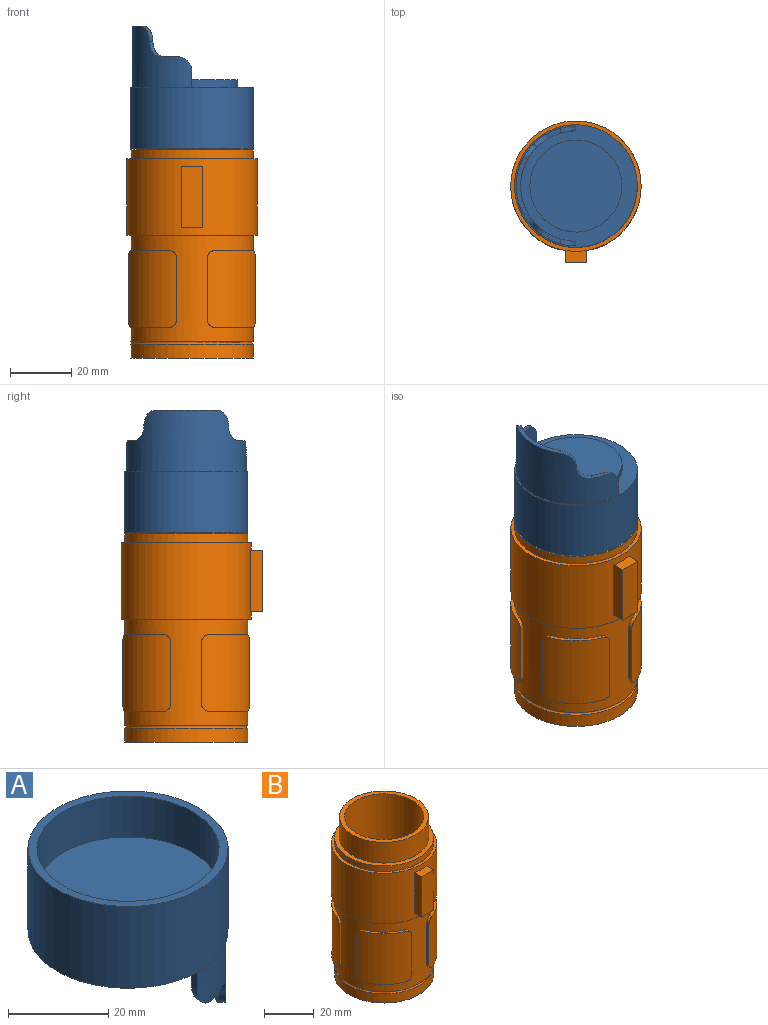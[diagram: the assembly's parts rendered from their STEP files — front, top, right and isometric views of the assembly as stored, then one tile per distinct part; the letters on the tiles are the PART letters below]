
ASSEMBLY  parts=2 mates=1
PART A: 20 faces, bbox 40x40x40 mm
  f0: plane 40x40mm, normal (0,0,-1), area 461.4mm2, adj f1,f5,f6,f8,f10,f18
  f1: cylinder r=20mm len=40mm, axis (0,0,-1), area 2513.3mm2, adj f0,f3
  f2: cylinder r=18.2mm len=36.4mm, axis (0,0,-1), area 1143.5mm2, adj f3,f4
  f3: plane 40x40mm, normal (0,0,1), area 216mm2, adj f1,f2
  f4: plane 36.4x36.4mm, normal (0,0,1), area 1040.6mm2, adj f2
  f5: cylinder r=18mm len=36mm, axis (0,0,1), area 837.5mm2, adj f0,f7,f8,f9,f10,f11,f12,f13
  f6: cylinder r=19.5mm len=39mm, axis (0,0,1), area 908.2mm2, adj f0,f7,f8,f9,f10,f11,f12,f13
  f7: plane 19.58x3.74mm, normal (0,0,-1), area 29mm2, adj f5,f6,f12,f16
  f8: plane 5x1.5mm, normal (-1,0,0), area 7.5mm2, adj f0,f5,f6,f14
  f9: plane 4.79x3.09mm, normal (0,0,-1), area 6.9mm2, adj f5,f6,f13,f14
  f10: plane 5x1.5mm, normal (-1,0,0), area 7.5mm2, adj f0,f5,f6,f15
  f11: plane 4.79x3.09mm, normal (0,0,-1), area 6.9mm2, adj f5,f6,f15,f17
  f12: cylinder r=5mm len=5.1mm, axis (0.71,-0.71,0), area 11.9mm2, adj f5,f6,f7,f13
  f13: cylinder r=5mm len=5.1mm, axis (-0.71,0.71,0), area 11.9mm2, adj f5,f6,f9,f12
  f14: cylinder r=5mm len=5mm, axis (0,-1,0), area 11.9mm2, adj f5,f6,f8,f9
  f15: cylinder r=5mm len=5mm, axis (0,-1,0), area 11.9mm2, adj f5,f6,f10,f11
  f16: cylinder r=5mm len=5.1mm, axis (-0.71,-0.71,0), area 11.9mm2, adj f5,f6,f7,f17
  f17: cylinder r=5mm len=5.1mm, axis (0.71,0.71,0), area 11.9mm2, adj f5,f6,f11,f16
  f18: cylinder r=15mm len=30mm, axis (0,0,1), area 235.6mm2, adj f0,f19
  f19: plane 30x30mm, normal (0,0,-1), area 706.9mm2, adj f18
PART B: 54 faces, bbox 44.1x47x78 mm
  f0: cylinder r=20mm len=40mm, axis (0,0,-1), area 351.9mm2, adj f5,f7
  f1: plane 36x36mm, normal (0,0,1), area 213.6mm2, adj f2,f4
  f2: cylinder r=16mm len=74mm, axis (0,0,-1), area 7439.3mm2, adj f1,f3
  f3: plane 32x32mm, normal (0,0,1), area 804.2mm2, adj f2
  f4: cylinder r=18mm len=36mm, axis (0,0,1), area 1153.6mm2, adj f1,f5
  f5: plane 40x40mm, normal (0,0,1), area 238.8mm2, adj f0,f4
  f6: cylinder r=21.25mm len=42.5mm, axis (0,0,-1), area 3197.3mm2, adj f7,f8,f49,f50,f51,f52
  f7: plane 42.5x42.5mm, normal (0,0,1), area 162mm2, adj f0,f6
  f8: plane 42.5x42.5mm, normal (0,0,-1), area 162mm2, adj f6,f48
  f9: plane 40x40mm, normal (0,0,-1), area 1256.6mm2, adj f14
  f10: cylinder r=21.25mm len=25mm, axis (0,0,-1), area 576.6mm2, adj f15,f16,f17,f18,f19,f20,f21,f22
  f11: cylinder r=21.25mm len=25mm, axis (0,0,-1), area 576.6mm2, adj f23,f24,f25,f26,f27,f28,f29,f30
  f12: cylinder r=21.25mm len=25mm, axis (0,0,-1), area 576.6mm2, adj f31,f32,f33,f34,f35,f36,f37,f38
  f13: cylinder r=21.25mm len=25mm, axis (0,0,-1), area 576.6mm2, adj f39,f40,f41,f42,f43,f44,f45,f46
  f14: cylinder r=20mm len=40mm, axis (0,0,-1), area 565.5mm2, adj f9,f47
  f15: cylinder r=2.5mm len=2.5mm, axis (0,-1,0), area 5.1mm2, adj f10,f16,f22,f48
  f16: plane 12.38x12.38mm, normal (0,0,-1), area 21.3mm2, adj f10,f15,f17,f48
  f17: cylinder r=2.5mm len=2.5mm, axis (-1,0,0), area 5.1mm2, adj f10,f16,f18,f48
  f18: plane 20x1.29mm, normal (0,1,0), area 25.8mm2, adj f10,f17,f19,f48
  f19: cylinder r=2.5mm len=2.5mm, axis (1,0,0), area 5.1mm2, adj f10,f18,f20,f48
  f20: plane 12.38x12.38mm, normal (0,0,1), area 21.3mm2, adj f10,f19,f21,f48
  f21: cylinder r=2.5mm len=2.5mm, axis (0,1,0), area 5.1mm2, adj f10,f20,f22,f48
  f22: plane 20x1.29mm, normal (-1,0,0), area 25.8mm2, adj f10,f15,f21,f48
  f23: cylinder r=2.5mm len=2.5mm, axis (1,0,0), area 5.1mm2, adj f11,f24,f30,f48
  f24: plane 12.38x12.38mm, normal (0,0,-1), area 21.3mm2, adj f11,f23,f25,f48
  f25: cylinder r=2.5mm len=2.5mm, axis (0,-1,0), area 5.1mm2, adj f11,f24,f26,f48
  f26: plane 20x1.29mm, normal (-1,0,0), area 25.8mm2, adj f11,f25,f27,f48
  f27: cylinder r=2.5mm len=2.5mm, axis (0,1,0), area 5.1mm2, adj f11,f26,f28,f48
  f28: plane 12.38x12.38mm, normal (0,0,1), area 21.3mm2, adj f11,f27,f29,f48
  f29: cylinder r=2.5mm len=2.5mm, axis (-1,0,0), area 5.1mm2, adj f11,f28,f30,f48
  f30: plane 20x1.29mm, normal (0,-1,0), area 25.8mm2, adj f11,f23,f29,f48
  f31: cylinder r=2.5mm len=2.5mm, axis (0,1,0), area 5.1mm2, adj f12,f32,f38,f48
  f32: plane 12.38x12.38mm, normal (0,0,-1), area 21.3mm2, adj f12,f31,f33,f48
  f33: cylinder r=2.5mm len=2.5mm, axis (1,0,0), area 5.1mm2, adj f12,f32,f34,f48
  f34: plane 20x1.29mm, normal (0,-1,0), area 25.8mm2, adj f12,f33,f35,f48
  f35: cylinder r=2.5mm len=2.5mm, axis (-1,0,0), area 5.1mm2, adj f12,f34,f36,f48
  f36: plane 12.38x12.38mm, normal (0,0,1), area 21.3mm2, adj f12,f35,f37,f48
  f37: cylinder r=2.5mm len=2.5mm, axis (0,-1,0), area 5.1mm2, adj f12,f36,f38,f48
  f38: plane 20x1.29mm, normal (1,0,0), area 25.8mm2, adj f12,f31,f37,f48
  f39: cylinder r=2.5mm len=2.5mm, axis (-1,0,0), area 5.1mm2, adj f13,f40,f46,f48
  f40: plane 12.38x12.38mm, normal (0,0,-1), area 21.3mm2, adj f13,f39,f41,f48
  f41: cylinder r=2.5mm len=2.5mm, axis (0,1,0), area 5.1mm2, adj f13,f40,f42,f48
  f42: plane 20x1.29mm, normal (1,0,0), area 25.8mm2, adj f13,f41,f43,f48
  f43: cylinder r=2.5mm len=2.5mm, axis (0,-1,0), area 5.1mm2, adj f13,f42,f44,f48
  f44: plane 12.38x12.38mm, normal (0,0,1), area 21.3mm2, adj f13,f43,f45,f48
  f45: cylinder r=2.5mm len=2.5mm, axis (1,0,0), area 5.1mm2, adj f13,f44,f46,f48
  f46: plane 20x1.29mm, normal (0,1,0), area 25.8mm2, adj f13,f39,f45,f48
  f47: torus R=20mm, axis (0,0,1), area 194.3mm2, adj f14,f48
  f48: cylinder r=20mm len=40mm, axis (0,0,-1), area 2226.9mm2, adj f8,f15,f16,f17,f18,f19,f20,f21
  f49: plane 20x4.04mm, normal (1,0,0), area 80.8mm2, adj f6,f51,f52,f53
  f50: plane 20x4.04mm, normal (-1,0,0), area 80.8mm2, adj f6,f51,f52,f53
  f51: plane 7x4.04mm, normal (0,0,-1), area 26.9mm2, adj f6,f49,f50,f53
  f52: plane 7x4.04mm, normal (0,0,1), area 26.9mm2, adj f6,f49,f50,f53
  f53: plane 20x7mm, normal (0,-1,0), area 140mm2, adj f49,f50,f51,f52
PLACE A rot(axis=(0,1,0),180deg) t=(-2.25,0.01,90.8)mm
PLACE B t=(-2.25,0.01,2.59)mm
MATE slider B.f0 <-> A.f1  axis (0,0,1) through (-2.25,0.01,80.59)mm
